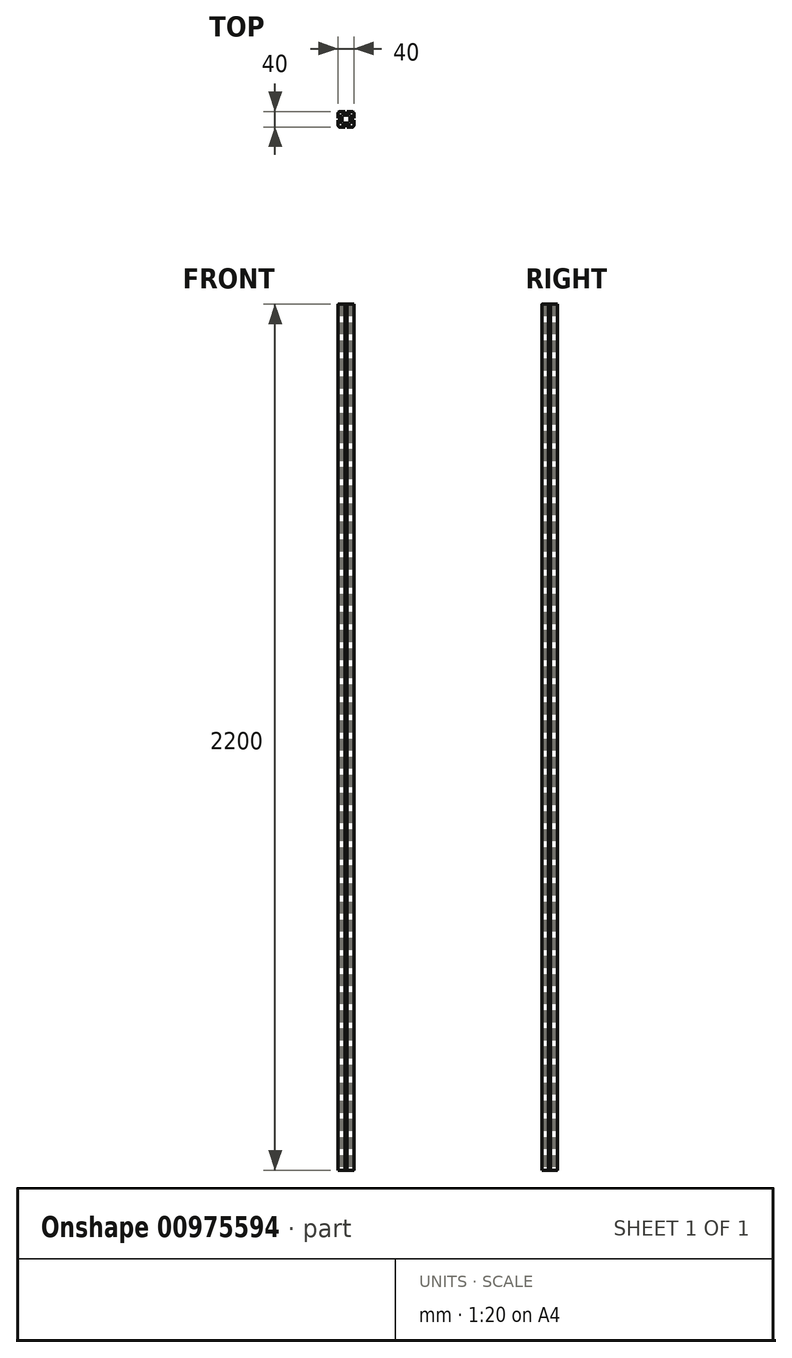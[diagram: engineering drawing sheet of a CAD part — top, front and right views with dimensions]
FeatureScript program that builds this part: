
annotation { "Feature Type Name" : "Feature", "Feature Type Description" : "" }
export const myFeature = defineFeature(function(context is Context, id is Id, definition is map)
    precondition{}
    {
        {
            var Q0;
            Q0=qCreatedBy(makeId("Top.planeOp"),FACE);
            var sketch = newSketch(context, id + "F0", { "sketchPlane" : qUnion([Q0])});
            skLineSegment(sketch, "E0", {"start": v(-15, 20) * mm, "end": v(-2.5, 20) * mm});
            skLineSegment(sketch, "E1", {"start": v(20, 15) * mm, "end": v(20, 2.5) * mm});
            skLineSegment(sketch, "E2", {"start": v(15, -20) * mm, "end": v(2.5, -20) * mm});
            skLineSegment(sketch, "E3", {"start": v(-20, -15) * mm, "end": v(-20, -2.5) * mm});
            skLineSegment(sketch, "E4", {"start": v(-2.5, 20) * mm, "end": v(-2.5, 15) * mm});
            skLineSegment(sketch, "E5", {"start": v(-2.5, 15) * mm, "end": v(-7.5, 15) * mm});
            skLineSegment(sketch, "E6", {"start": v(-7.5, 15) * mm, "end": v(-7.5, 10) * mm});
            skLineSegment(sketch, "E7", {"start": v(-7.5, 10) * mm, "end": v(7.5, 10) * mm});
            skLineSegment(sketch, "E8", {"start": v(7.5, 10) * mm, "end": v(7.5, 15) * mm});
            skLineSegment(sketch, "E9", {"start": v(7.5, 15) * mm, "end": v(2.5, 15) * mm});
            skLineSegment(sketch, "E10", {"start": v(2.5, 15) * mm, "end": v(2.5, 20) * mm});
            skLineSegment(sketch, "E11.trimOffspring", {"start": v(2.5, 20) * mm, "end": v(15, 20) * mm});
            skLineSegment(sketch, "E12", {"start": v(20, 2.5) * mm, "end": v(15, 2.5) * mm});
            skLineSegment(sketch, "E13", {"start": v(15, 2.5) * mm, "end": v(15, 7.5) * mm});
            skLineSegment(sketch, "E14", {"start": v(15, 7.5) * mm, "end": v(10, 7.5) * mm});
            skLineSegment(sketch, "E15", {"start": v(10, 7.5) * mm, "end": v(10, -7.5) * mm});
            skLineSegment(sketch, "E16", {"start": v(10, -7.5) * mm, "end": v(15, -7.5) * mm});
            skLineSegment(sketch, "E17", {"start": v(15, -7.5) * mm, "end": v(15, -2.5) * mm});
            skLineSegment(sketch, "E18", {"start": v(15, -2.5) * mm, "end": v(20, -2.5) * mm});
            skLineSegment(sketch, "E19.trimOffspring", {"start": v(20, -2.5) * mm, "end": v(20, -15) * mm});
            skLineSegment(sketch, "E20", {"start": v(-2.5, -20) * mm, "end": v(-2.5, -15) * mm});
            skLineSegment(sketch, "E21", {"start": v(-2.5, -15) * mm, "end": v(-7.5, -15) * mm});
            skLineSegment(sketch, "E22", {"start": v(-7.5, -15) * mm, "end": v(-7.5, -10) * mm});
            skLineSegment(sketch, "E23", {"start": v(-7.5, -10) * mm, "end": v(7.5, -10) * mm});
            skLineSegment(sketch, "E24", {"start": v(7.5, -10) * mm, "end": v(7.5, -15) * mm});
            skLineSegment(sketch, "E25", {"start": v(7.5, -15) * mm, "end": v(2.5, -15) * mm});
            skLineSegment(sketch, "E26", {"start": v(2.5, -15) * mm, "end": v(2.5, -20) * mm});
            skPoint(sketch, "E27.orphan", {"position": v(-2.5, -25.12) * mm});
            skLineSegment(sketch, "E28.trimOffspring", {"start": v(-2.5, -20) * mm, "end": v(-15, -20) * mm});
            skLineSegment(sketch, "E29", {"start": v(-20, -2.5) * mm, "end": v(-15, -2.5) * mm});
            skLineSegment(sketch, "E30", {"start": v(-15, -2.5) * mm, "end": v(-15, -7.5) * mm});
            skLineSegment(sketch, "E31", {"start": v(-15, -7.5) * mm, "end": v(-10, -7.5) * mm});
            skLineSegment(sketch, "E32", {"start": v(-10, -7.5) * mm, "end": v(-10, 7.5) * mm});
            skPoint(sketch, "E32.endSnap0", {"position": v(12.5, 7.5) * mm});
            skLineSegment(sketch, "E33", {"start": v(-10, 7.5) * mm, "end": v(-15, 7.5) * mm});
            skPoint(sketch, "E33.endSnap0", {"position": v(-15, -5) * mm});
            skLineSegment(sketch, "E34", {"start": v(-15, 7.5) * mm, "end": v(-15, 2.5) * mm});
            skPoint(sketch, "E34.endSnap0", {"position": v(17.5, 2.5) * mm});
            skLineSegment(sketch, "E35", {"start": v(-15, 2.5) * mm, "end": v(-20, 2.5) * mm});
            skPoint(sketch, "E36.orphan", {"position": v(-25.65, -2.5) * mm});
            skLineSegment(sketch, "E37.trimOffspring", {"start": v(-20, 2.5) * mm, "end": v(-20, 15) * mm});
            skPoint(sketch, "E38.visualSharp", {"position": v(20, 20) * mm});
            skArc(sketch, "E38.filletArc", {"start": v(20, 15) * mm, "mid": v(18.54, 18.54) * mm, "end": v(15, 20) * mm});
            skPoint(sketch, "E39.visualSharp", {"position": v(20, -20) * mm});
            skArc(sketch, "E39.filletArc", {"start": v(15, -20) * mm, "mid": v(18.54, -18.54) * mm, "end": v(20, -15) * mm});
            skPoint(sketch, "E40.visualSharp", {"position": v(-20, -20) * mm});
            skArc(sketch, "E40.filletArc", {"start": v(-20, -15) * mm, "mid": v(-18.54, -18.54) * mm, "end": v(-15, -20) * mm});
            skPoint(sketch, "E41.visualSharp", {"position": v(-20, 20) * mm});
            skArc(sketch, "E41.filletArc", {"start": v(-15, 20) * mm, "mid": v(-18.54, 18.54) * mm, "end": v(-20, 15) * mm});
            skSolve(sketch);
        }
        {
            var Q0;
            Q0 = qSketchRegion(id + "F0", true);
            extrude(context, id + "F1", {"entities" : qUnion([Q0]), "depth" : 2200 * mm, "offsetDistance" : 25 * mm});
        }
    });
